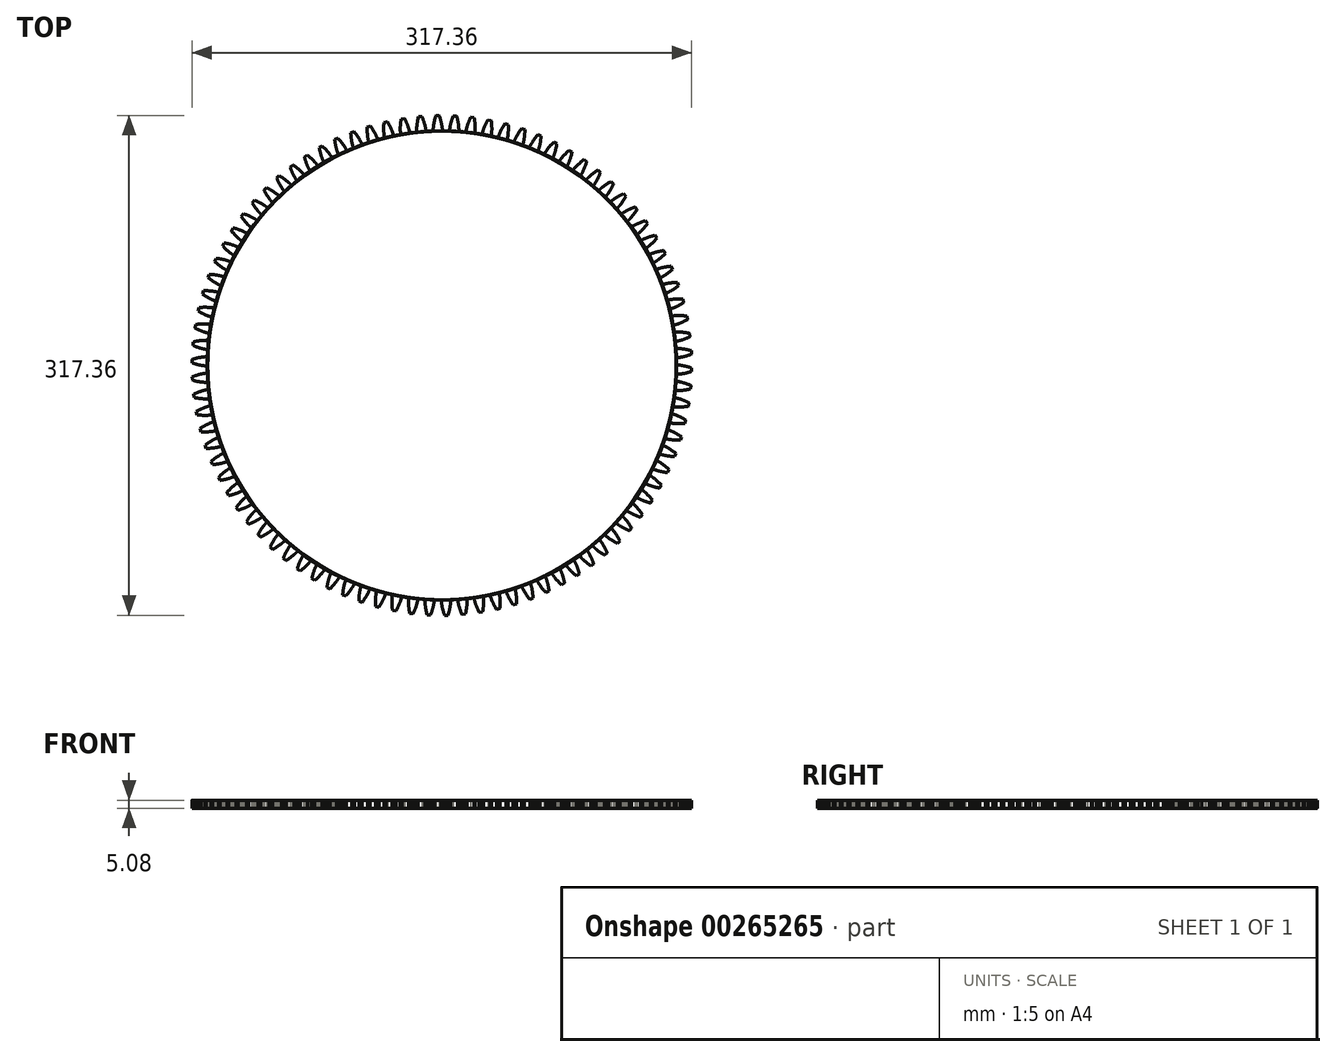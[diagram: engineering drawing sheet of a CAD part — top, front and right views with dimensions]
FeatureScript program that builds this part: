
annotation { "Feature Type Name" : "Feature", "Feature Type Description" : "" }
export const myFeature = defineFeature(function(context is Context, id is Id, definition is map)
    precondition{}
    {
        {
            var Q0;
            Q0=qCreatedBy(makeId("Top.planeOp"),FACE);
            var sketch = newSketch(context, id + "F0", { "sketchPlane" : qUnion([Q0])});
            skCircle(sketch, "E0", {"center": v(0, 0) * mm, "radius": 148.97 * mm});
            skCircle(sketch, "E1", {"center": v(0, 0) * mm, "radius": 152.4 * mm, "construction": true});
            skCircle(sketch, "E2", {"center": v(0, 0) * mm, "radius": 158.75 * mm, "construction": true});
            skLineSegment(sketch, "E3", {"start": v(0, 0) * mm, "end": v(0, 250.74) * mm, "construction": true});
            skLineSegment(sketch, "E4", {"start": v(0, 0) * mm, "end": v(-4.15, 237.56) * mm, "construction": true});
            skLineSegment(sketch, "E5", {"start": v(0, 152.4) * mm, "end": v(-219.5, 148.57) * mm, "construction": true});
            skLineSegment(sketch, "E6", {"start": v(0, 152.4) * mm, "end": v(-232.58, 115.56) * mm, "construction": true});
            skCircle(sketch, "E7", {"center": v(0, 152.4) * mm, "radius": 38.1 * mm, "construction": true});
            skCircle(sketch, "E8", {"center": v(0, 0) * mm, "radius": 150.52 * mm, "construction": true});
            skCircle(sketch, "E9", {"center": v(-37.52, 145.77) * mm, "radius": 38.1 * mm, "construction": true});
            skArc(sketch, "E10", {"start": v(0, 152.4) * mm, "mid": v(-0.71, 155.57) * mm, "end": v(-1.67, 158.68) * mm});
            skArc(sketch, "E11", {"start": v(0.45, 148.97) * mm, "mid": v(0.23, 150.69) * mm, "end": v(0, 152.4) * mm});
            skArc(sketch, "E12.MirrorCS", {"start": v(-5.32, 152.3) * mm, "mid": v(-4.72, 155.5) * mm, "end": v(-3.87, 158.64) * mm});
            skArc(sketch, "E13.MirrorCS", {"start": v(-5.65, 148.86) * mm, "mid": v(-5.49, 150.59) * mm, "end": v(-5.32, 152.3) * mm});
            skLineSegment(sketch, "E14", {"start": v(-3.87, 158.64) * mm, "end": v(-1.67, 158.68) * mm});
            skSolve(sketch);
        }
        {
            var Q0;
            Q0 = qSketchRegion(id + "F0", true);
            extrude(context, id + "F1", {"entities" : qUnion([Q0]), "depth" : 5.08 * mm});
        }
        {
            var Q0;
            Q0=makeQuery(id+"F1.opExtrude","SWEPT_BODY",BODY,{"disambiguationData":[OSD([sQuery(id+"F0.wireOp",EDGE,"E0"),sQuery(id+"F0.wireOp",EDGE,"E10"),sQuery(id+"F0.wireOp",EDGE,"E11"),sQuery(id+"F0.wireOp",EDGE,"E12.MirrorCS"),sQuery(id+"F0.wireOp",EDGE,"E13.MirrorCS"),sQuery(id+"F0.wireOp",EDGE,"E14")])]});
            var Q1;
            Q1=makeQuery(id+"F1.opExtrude","SWEPT_FACE",FACE,{"disambiguationData":[OSD([sQuery(id+"F0.wireOp",EDGE,"E0")])]});
            circularPattern(context, id + "F2", {"entities" : qUnion([Q0]), "axis" : qUnion([Q1]), "angle" : 360 * degree, "instanceCount" : 90, "equalSpace" : true});
        }
    });
